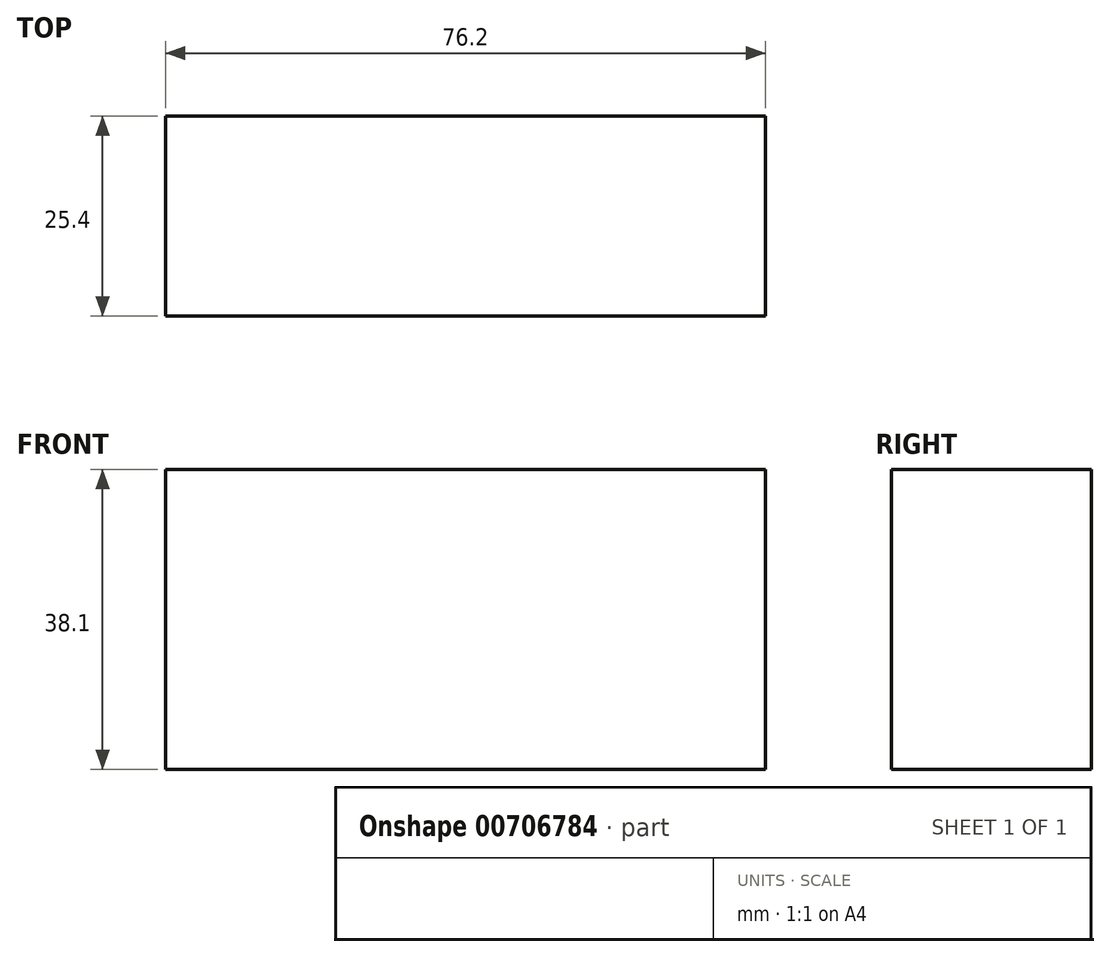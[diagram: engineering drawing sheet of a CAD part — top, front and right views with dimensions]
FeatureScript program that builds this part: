
annotation { "Feature Type Name" : "Feature", "Feature Type Description" : "" }
export const myFeature = defineFeature(function(context is Context, id is Id, definition is map)
    precondition{}
    {
        {
            var Q0;
            Q0=qCreatedBy(makeId("Front.planeOp"),FACE);
            var sketch = newSketch(context, id + "F0", { "sketchPlane" : qUnion([Q0])});
            skLineSegment(sketch, "E0.bottom", {"start": v(-38.1, 19.05) * mm, "end": v(38.1, 19.05) * mm});
            skLineSegment(sketch, "E0.top", {"start": v(-38.1, -19.05) * mm, "end": v(38.1, -19.05) * mm});
            skLineSegment(sketch, "E0.left", {"start": v(-38.1, 19.05) * mm, "end": v(-38.1, -19.05) * mm});
            skLineSegment(sketch, "E0.right", {"start": v(38.1, 19.05) * mm, "end": v(38.1, -19.05) * mm});
            skSolve(sketch);
        }
        {
            var Q0;
            Q0=makeQuery(id+"F0.imprint","IMPRINT",FACE,{"disambiguationData":[TD([[makeQuery(id+"F0.imprint","IMPRINT",EDGE,{"derivedFrom":sQuery(id+"F0.wireOp",EDGE,"E0.bottom")}),-1.0]])]});
            extrude(context, id + "F1", {"entities" : qUnion([Q0]), "depth" : 25.4 * mm, "offsetDistance" : 25.4 * mm});
        }
    });
